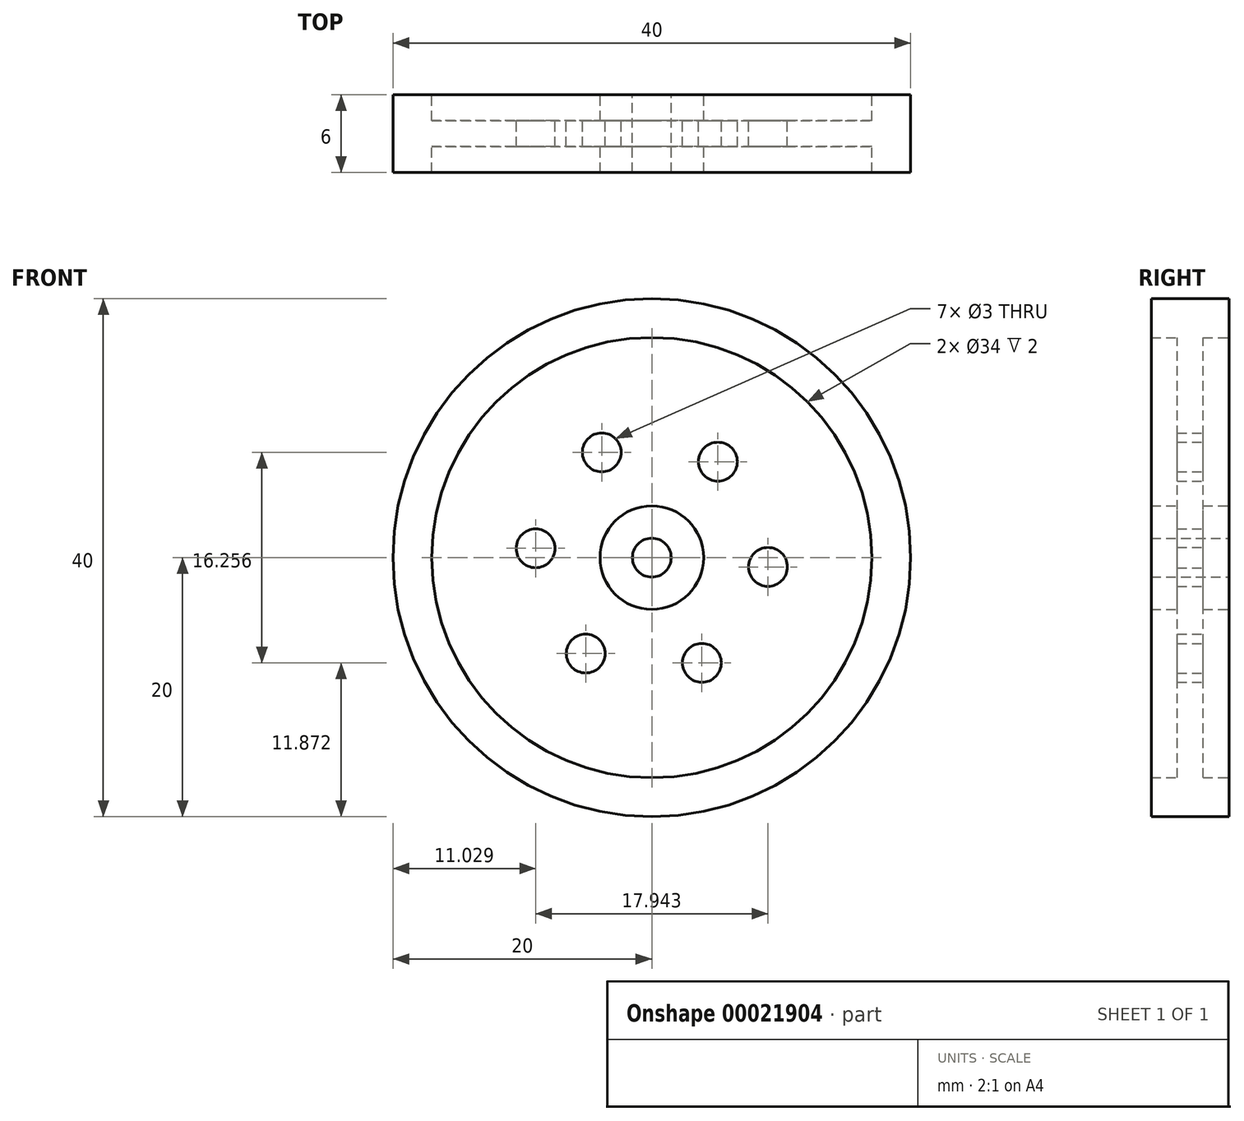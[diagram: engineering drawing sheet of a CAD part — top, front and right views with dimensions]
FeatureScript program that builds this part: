
annotation { "Feature Type Name" : "Feature", "Feature Type Description" : "" }
export const myFeature = defineFeature(function(context is Context, id is Id, definition is map)
    precondition{}
    {
        {
            var Q0;
            Q0=qCreatedBy(makeId("Front.planeOp"),FACE);
            var sketch = newSketch(context, id + "F0", { "sketchPlane" : qUnion([Q0])});
            skCircle(sketch, "E0", {"center": v(0, 0) * mm, "radius": 20 * mm});
            skCircle(sketch, "E1", {"center": v(0, 0) * mm, "radius": 17 * mm});
            skCircle(sketch, "E2", {"center": v(0, 0) * mm, "radius": 4 * mm});
            skCircle(sketch, "E3", {"center": v(0, 0) * mm, "radius": 1.5 * mm});
            skCircle(sketch, "E4", {"center": v(5.1, 7.41) * mm, "radius": 1.5 * mm});
            skCircle(sketch, "E5.1.0", {"center": v(-3.86, 8.13) * mm, "radius": 1.5 * mm});
            skCircle(sketch, "E5.2.0", {"center": v(-8.97, 0.72) * mm, "radius": 1.5 * mm});
            skCircle(sketch, "E5.3.0", {"center": v(-5.1, -7.41) * mm, "radius": 1.5 * mm});
            skCircle(sketch, "E5.4.0", {"center": v(3.86, -8.13) * mm, "radius": 1.5 * mm});
            skCircle(sketch, "E5.5.0", {"center": v(8.97, -0.72) * mm, "radius": 1.5 * mm});
            skSolve(sketch);
        }
        {
            var Q0;
            Q0 = qSketchRegion(id + "F0", true);
            var Q1;
            Q1=makeQuery(id+"F0.imprint","IMPRINT",FACE,{"disambiguationData":[TD([[makeQuery(id+"F0.imprint","IMPRINT",EDGE,{"derivedFrom":sQuery(id+"F0.wireOp",EDGE,"E2")}),1.0]])]});
            extrude(context, id + "F1", {"entities" : qUnion([Q0, Q1]), "depth" : 6 * mm});
        }
        {
            var Q0;
            Q0=makeQuery(id+"F0.imprint","IMPRINT",FACE,{"disambiguationData":[TD([[makeQuery(id+"F0.imprint","IMPRINT",EDGE,{"derivedFrom":sQuery(id+"F0.wireOp",EDGE,"E1")}),1.0]])]});
            extrude(context, id + "F2", {"entities" : qUnion([Q0]), "operationType" : NewBodyOperationType.ADD, "depth" : 4 * mm});
        }
        {
            var Q0;
            Q0=makeQuery(id+"F0.imprint","IMPRINT",FACE,{"disambiguationData":[TD([[makeQuery(id+"F0.imprint","IMPRINT",EDGE,{"derivedFrom":sQuery(id+"F0.wireOp",EDGE,"E1")}),1.0]])]});
            extrude(context, id + "F3", {"entities" : qUnion([Q0]), "operationType" : NewBodyOperationType.REMOVE, "depth" : 2 * mm});
        }
    });
